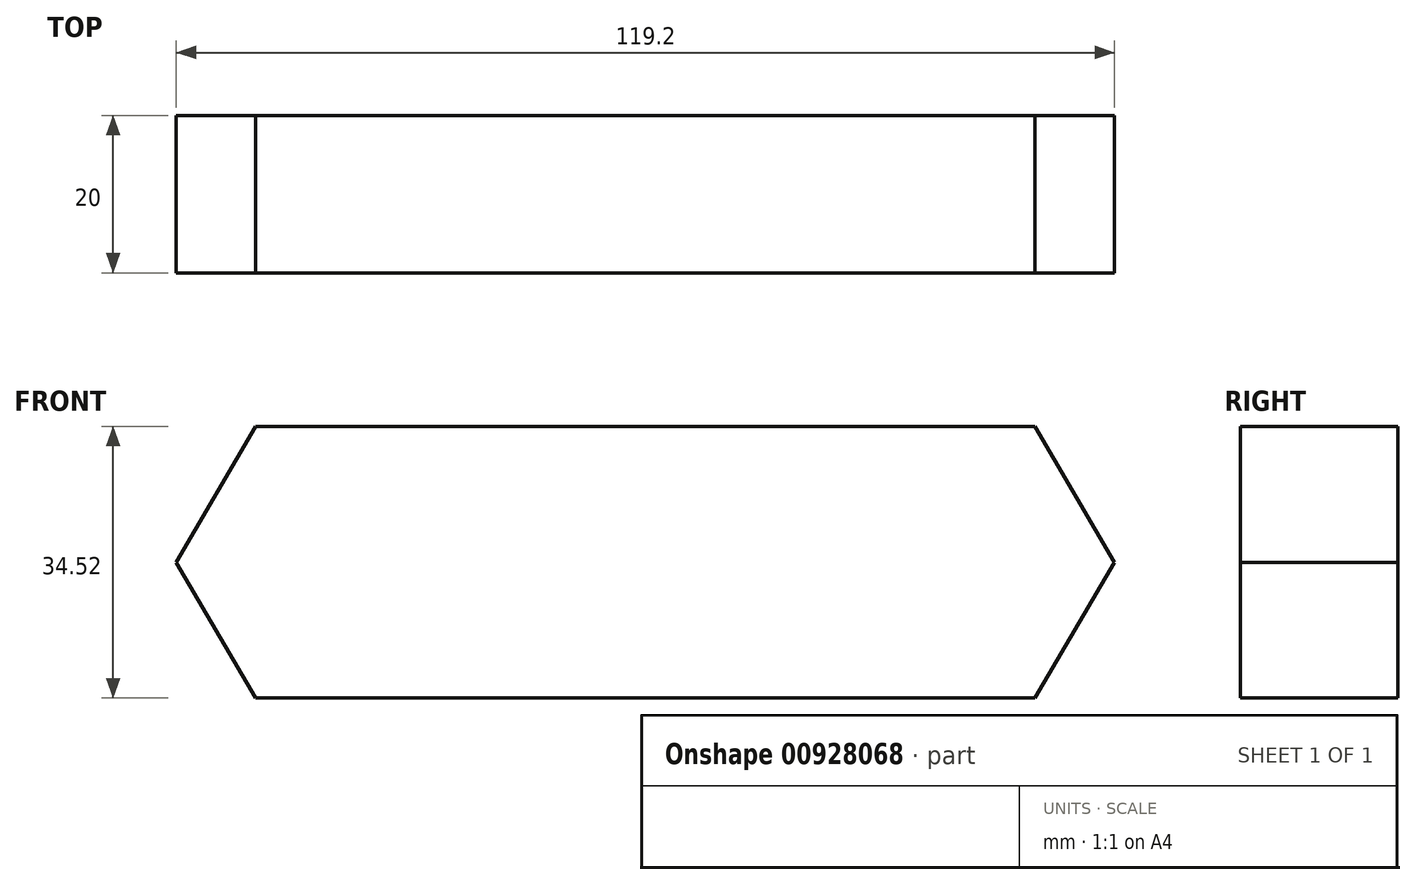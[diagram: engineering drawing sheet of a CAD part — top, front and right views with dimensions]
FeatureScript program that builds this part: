
annotation { "Feature Type Name" : "Feature", "Feature Type Description" : "" }
export const myFeature = defineFeature(function(context is Context, id is Id, definition is map)
    precondition{}
    {
        {
            var Q0;
            Q0=qCreatedBy(makeId("Front.planeOp"),FACE);
            var sketch = newSketch(context, id + "F0", { "sketchPlane" : qUnion([Q0])});
            skLineSegment(sketch, "E0", {"start": v(-109.1, 0) * mm, "end": v(10.1, 0) * mm});
            skLineSegment(sketch, "E1", {"start": v(-109.1, 0) * mm, "end": v(-99, 17.26) * mm});
            skLineSegment(sketch, "E2", {"start": v(-99, 17.26) * mm, "end": v(0, 17.26) * mm});
            skLineSegment(sketch, "E3", {"start": v(0, 17.26) * mm, "end": v(10.1, 0) * mm});
            skLineSegment(sketch, "E4.MirrorCS", {"start": v(-99, -17.26) * mm, "end": v(0, -17.26) * mm});
            skLineSegment(sketch, "E5.MirrorCS", {"start": v(-109.1, 0) * mm, "end": v(-99, -17.26) * mm});
            skLineSegment(sketch, "E6.MirrorCS", {"start": v(0, -17.26) * mm, "end": v(10.1, 0) * mm});
            skSolve(sketch);
        }
        {
            var Q0;
            Q0 = qSketchRegion(id + "F0", true);
            extrude(context, id + "F1", {"entities" : qUnion([Q0]), "depth" : 20 * mm, "offsetDistance" : 25 * mm});
        }
    });
